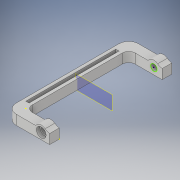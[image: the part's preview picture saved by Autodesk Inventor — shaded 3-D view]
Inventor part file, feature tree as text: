
AUTODESK INVENTOR PART (.ipt)
format: ipt  version: 2018 (Build 220112000, 112)  size: 390,656 bytes
history: native  units: in
note: dims shown in document units (in); Inventor stores cm internally (conversion verified against a paired STEP export)
features: sketch x17, extrude x10, fillet x6, hole x2, plane x1, mirror x1
ambient origin geometry x8: Origin, YZ Plane, XZ Plane, XY Plane, X Axis, Y Axis, Z Axis, Center Point
bodies: Solid1 (feature_tree)
feature tree (37):
  extrude  "Extrusion1"  Depth=0.375in
  sketch  "Sketch2"  dims[d3=0.375in d4=0.5in d5=0.375in d6=0.0in]
  extrude  "Extrusion2"  Depth=0.375in
  fillet  "Fillet1"  Radius=0.375in
  extrude  "Extrusion3"  Depth=0.375in
  extrude  "Extrusion4"  Depth=0.25in
  plane  "Work Plane1"
  mirror  "Mirror1"
  fillet  "Fillet2"  Radius=0.24in
  extrude  "Extrusion5"  Depth=0.375in
  sketch  "Sketch6"  dims[d17=1.0in d18=0.0in d19=0.24in d20=0.0in]
  extrude  "Extrusion6"  Depth=0.24in TaperAngle=0.0deg
  extrude  "Extrusion7"  Depth=0.375in
  fillet  "Fillet3"  Radius=0.25in
  fillet  "Fillet4"  Radius=0.375in
  fillet  "Fillet5"  Radius=0.25in
  fillet  "Fillet6"  Radius=0.125in
  sketch  "Sketch9"  dims[d30=0.125in d31=0.125in]
  extrude  "Extrusion8"  Depth=0.035in
  sketch  "Sketch11"  dims[d35=0.2in]
  sketch  "Sketch12"  dims[d36=0.2in d37=0.75in d38=0.375in d39=0.25in d40=0.5635in d41=0.35in d42=0.0in]
  hole  "Hole1"  [1 undecoded]
  hole  "Hole2"  [1 undecoded]
  sketch  "Sketch14"  dims[d51=3.5in d52=0.375in d53=0.0in]
  extrude  "Extrusion9"  Depth=0.125in
  extrude  "Extrusion10"  Depth=0.375in TaperAngle=0.0deg
  sketch  "Sketch17"
  sketch  "Sketch1"  dims[d0=1.3in d1=0.375in]
  sketch  "Sketch3"  dims[d7=0.375in d8=0.0in d9=0.375in]
  sketch  "Sketch4"  dims[d10=0.24in d11=0.0in d12=0.25in d13=0.24in d14=0.0in]
  sketch  "Sketch5"  dims[d15=2.0in d16=0.375in]
  sketch  "Sketch7"  dims[d21=0.375in d22=0.0in d23=0.375in d24=0.25in d25=0.375in d26=0.25in d27=0.125in]
  sketch  "Sketch8"  dims[d28=0.035in d29=0.035in]
  sketch  "Sketch10"  dims[d32=4.375in d33=0.0in d34=0.2in]
  sketch  "Sketch13"  dims[d43=0.2in d44=0.75in d45=0.375in d46=0.25in d47=0.5635in d48=0.35in d49=0.0in d50=0.125in]
  sketch  "Sketch15"  dims[d54=1.0in d55=0.0in]
  sketch  "Sketch16"
note: 2 required parameter values undecoded (feature->parameter linkage not recoverable at this tier; creation-order binding heuristic only, values carry confidence <= 0.55)
